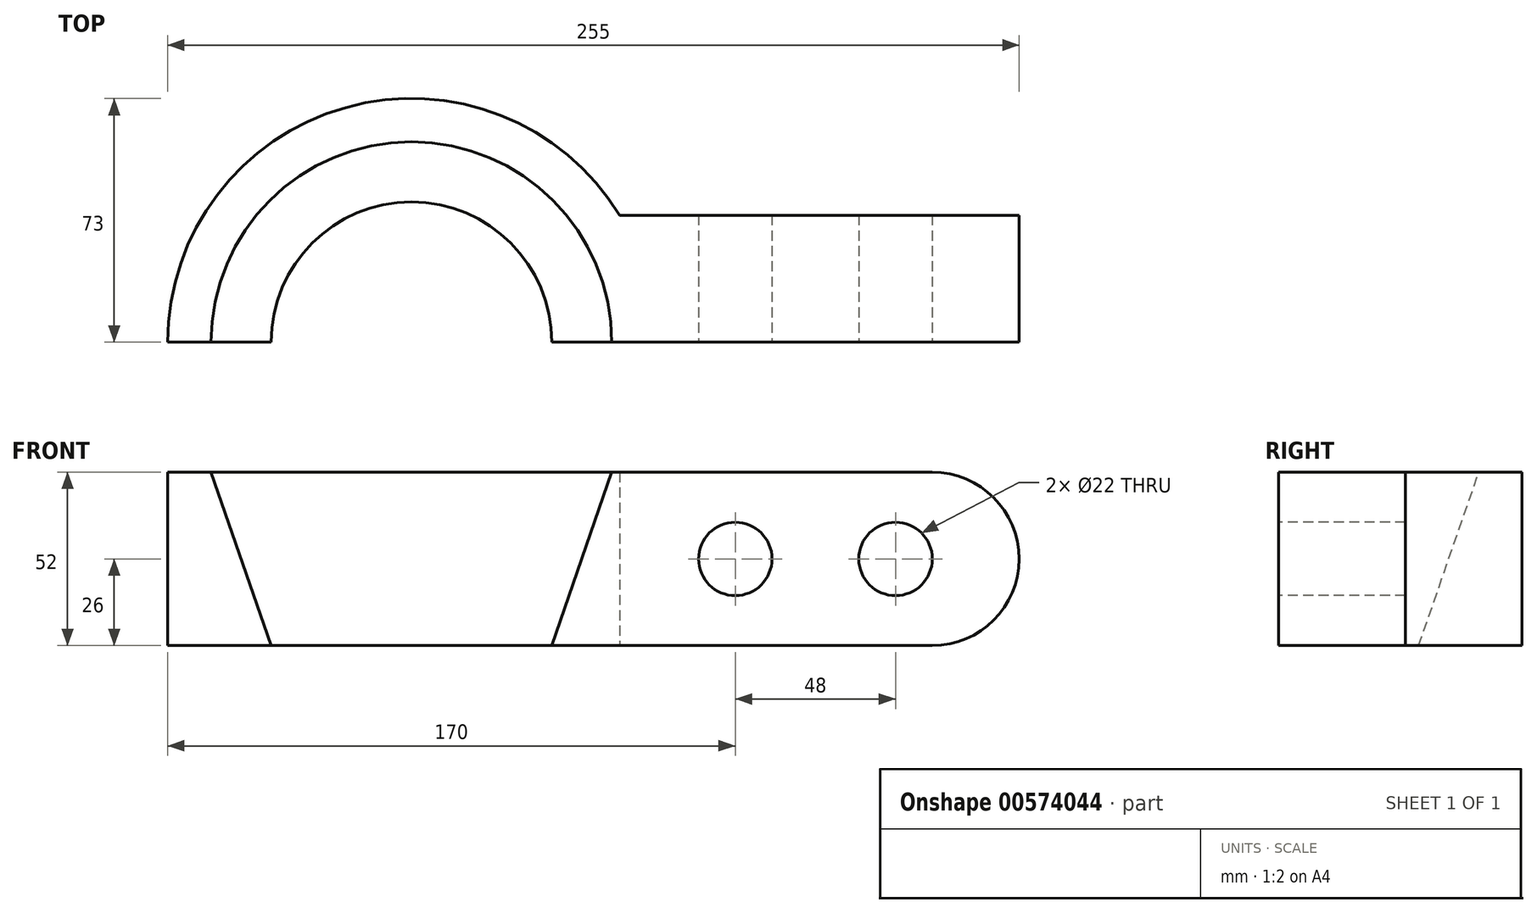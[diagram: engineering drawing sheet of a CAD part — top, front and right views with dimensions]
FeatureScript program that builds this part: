
annotation { "Feature Type Name" : "Feature", "Feature Type Description" : "" }
export const myFeature = defineFeature(function(context is Context, id is Id, definition is map)
    precondition{}
    {
        {
            var Q0;
            Q0=qCreatedBy(makeId("Top.planeOp"),FACE);
            var sketch = newSketch(context, id + "F0", { "sketchPlane" : qUnion([Q0])});
            skArc(sketch, "E0", {"start": v(62.33, 38) * mm, "mid": v(-19.73, 70.28) * mm, "end": v(-73, 0) * mm});
            skArc(sketch, "E1", {"start": v(21, 0) * mm, "mid": v(0, 21) * mm, "end": v(-21, 0) * mm});
            skLineSegment(sketch, "E2.bottom", {"start": v(73, 0) * mm, "end": v(182, 0) * mm});
            skLineSegment(sketch, "E2.top", {"start": v(62.33, 38) * mm, "end": v(182, 38) * mm});
            skLineSegment(sketch, "E2.right", {"start": v(182, 0) * mm, "end": v(182, 38) * mm});
            skLineSegment(sketch, "E3", {"start": v(-93.91, 0) * mm, "end": v(246.3, 0) * mm, "construction": true});
            skLineSegment(sketch, "E4", {"start": v(-73, 0) * mm, "end": v(-21, 0) * mm});
            skLineSegment(sketch, "E5", {"start": v(21, 0) * mm, "end": v(73, 0) * mm});
            skSolve(sketch);
        }
        {
            var Q0;
            Q0=makeQuery(id+"F0.imprint","IMPRINT",FACE,{"disambiguationData":[TD([[makeQuery(id+"F0.imprint","IMPRINT",EDGE,{"derivedFrom":sQuery(id+"F0.wireOp",EDGE,"E0")}),1.0]])]});
            extrude(context, id + "F1", {"entities" : qUnion([Q0]), "depth" : 52 * mm, "offsetDistance" : 25 * mm});
        }
        {
            var Q0;
            Q0=makeQuery(id+"F1.opExtrude","SWEPT_FACE",FACE,{"disambiguationData":[OSD([sQuery(id+"F0.wireOp",EDGE,"E4")])]});
            var sketch = newSketch(context, id + "F2", { "sketchPlane" : qUnion([Q0])});
            skLineSegment(sketch, "E6", {"start": v(-60, 52) * mm, "end": v(-42, 0) * mm});
            skLineSegment(sketch, "E7", {"start": v(-42, 0) * mm, "end": v(0, 0) * mm});
            skLineSegment(sketch, "E8", {"start": v(0, 0) * mm, "end": v(0, 52) * mm});
            skLineSegment(sketch, "E9", {"start": v(0, 52) * mm, "end": v(-60, 52) * mm});
            skSolve(sketch);
        }
        {
            var Q0;
            {var subQ0=sQuery(id+"F2.wireOp",EDGE,"E6");Q0=makeQuery(id+"F2.imprint","IMPRINT",FACE,{"disambiguationData":[TD([[makeQuery(id+"F2.imprint","IMPRINT",EDGE,{"derivedFrom":subQ0}),1.0]])]});}
            var Q1;
            {var subQ2=sQuery(id+"F2.wireOp",EDGE,"E8");Q1=makeQuery(id+"F2.imprint","IMPRINT",FACE,{"disambiguationData":[TD([[makeQuery(id+"F2.imprint","IMPRINT",EDGE,{"derivedFrom":subQ2}),1.0]])]});}
            var Q2;
            Q2=sQuery(id+"F2.wireOp",EDGE,"E8");
            revolve(context, id + "F3", {"operationType" : NewBodyOperationType.REMOVE, "entities" : qUnion([Q0, Q1]), "axis" : qUnion([Q2]), "revolveType" : RevolveType.FULL, "oppositeDirection" : true});
        }
        {
            var Q0;
            Q0=makeQuery(id+"F1.opExtrude","SWEPT_FACE",FACE,{"disambiguationData":[OSD([sQuery(id+"F0.wireOp",EDGE,"E2.bottom"),sQuery(id+"F0.wireOp",EDGE,"E5")])]});
            var sketch = newSketch(context, id + "F4", { "sketchPlane" : qUnion([Q0])});
            skCircle(sketch, "E10", {"center": v(97, 26) * mm, "radius": 11 * mm});
            skCircle(sketch, "E11", {"center": v(145, 26) * mm, "radius": 11 * mm});
            skSolve(sketch);
        }
        {
            var Q0;
            Q0=makeQuery(id+"F4.imprint","IMPRINT",FACE,{"disambiguationData":[TD([[makeQuery(id+"F4.imprint","IMPRINT",EDGE,{"derivedFrom":sQuery(id+"F4.wireOp",EDGE,"E10")}),1.0]])]});
            var Q1;
            Q1=makeQuery(id+"F4.imprint","IMPRINT",FACE,{"disambiguationData":[TD([[makeQuery(id+"F4.imprint","IMPRINT",EDGE,{"derivedFrom":sQuery(id+"F4.wireOp",EDGE,"E11")}),1.0]])]});
            extrude(context, id + "F5", {"entities" : qUnion([Q0, Q1]), "operationType" : NewBodyOperationType.REMOVE, "oppositeDirection" : true, "depth" : 88.3 * mm, "offsetDistance" : 25 * mm});
        }
        {
            var Q0;
            Q0=makeQuery(id+"F1.opExtrude","CAP_EDGE",EDGE,{"disambiguationData":[OSD([sQuery(id+"F0.wireOp",EDGE,"E2.right")])],"isStart":false});
            var Q1;
            Q1=makeQuery(id+"F1.opExtrude","CAP_EDGE",EDGE,{"disambiguationData":[OSD([sQuery(id+"F0.wireOp",EDGE,"E2.right")])],"isStart":true});
            fillet(context, id + "F6", {"entities" : qUnion([Q0, Q1]), "radius" : 26 * mm, "tangentPropagation" : true, "allowEdgeOverflow" : false});
        }
    });
